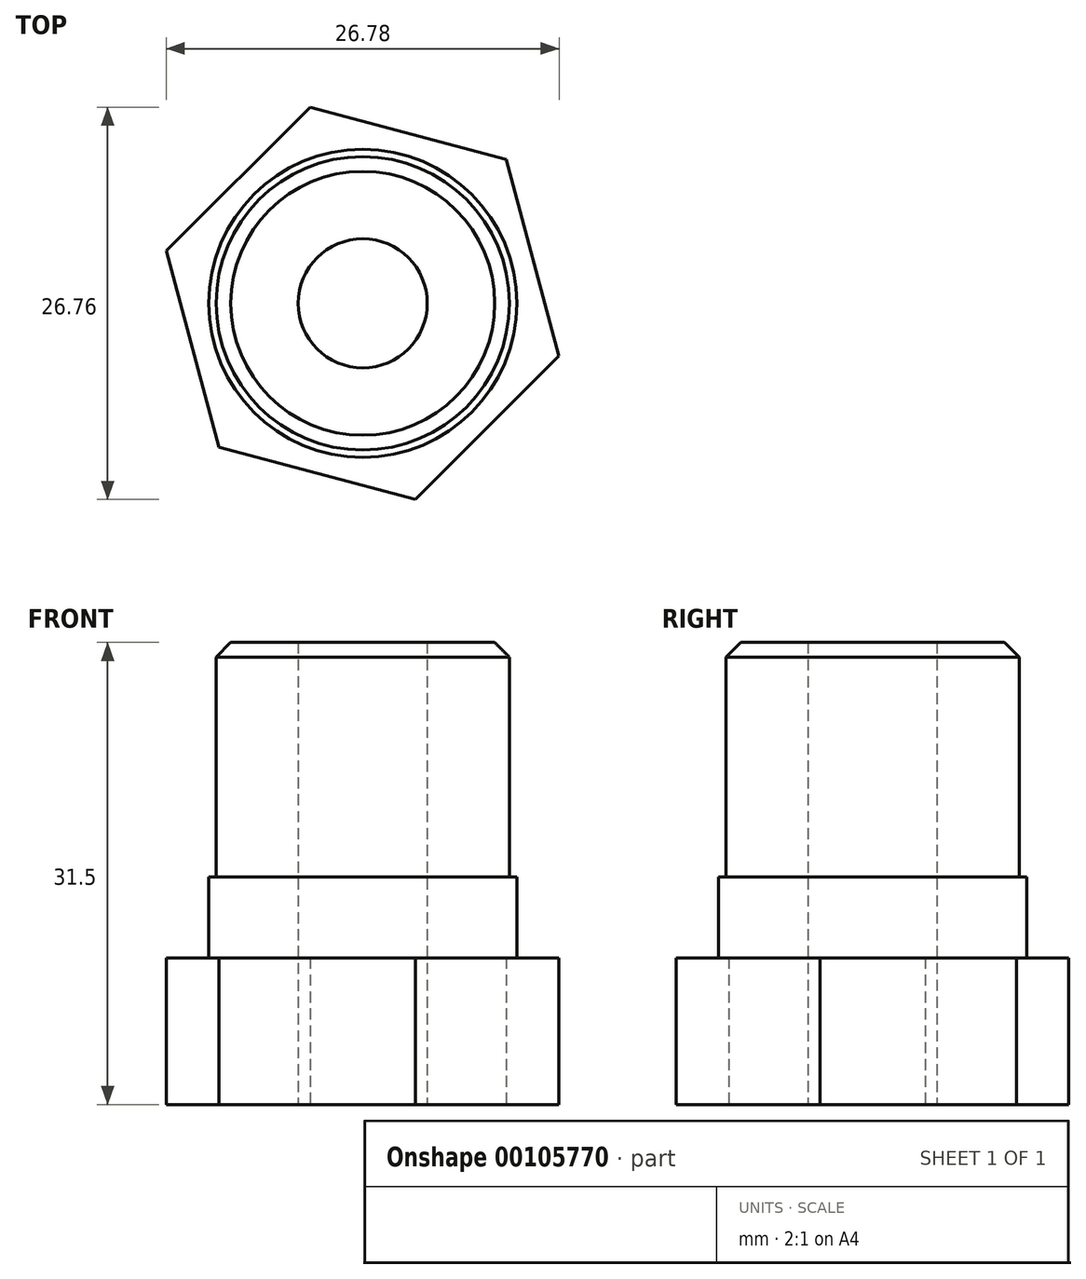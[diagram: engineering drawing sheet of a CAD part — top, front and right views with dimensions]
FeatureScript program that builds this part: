
annotation { "Feature Type Name" : "Feature", "Feature Type Description" : "" }
export const myFeature = defineFeature(function(context is Context, id is Id, definition is map)
    precondition{}
    {
        {
            var Q0;
            Q0=qCreatedBy(makeId("Top.planeOp"),FACE);
            var sketch = newSketch(context, id + "F0", { "sketchPlane" : qUnion([Q0])});
            skCircle(sketch, "E0.cCircle", {"center": v(0, 0) * mm, "radius": 12 * mm, "construction": true});
            skLineSegment(sketch, "E0.0", {"start": v(13.39, -3.58) * mm, "end": v(3.6, -13.38) * mm});
            skLineSegment(sketch, "E0.1", {"start": v(3.6, -13.38) * mm, "end": v(-9.8, -9.8) * mm});
            skLineSegment(sketch, "E0.2", {"start": v(-9.8, -9.8) * mm, "end": v(-13.39, 3.58) * mm});
            skLineSegment(sketch, "E0.3", {"start": v(-13.39, 3.58) * mm, "end": v(-3.6, 13.38) * mm});
            skLineSegment(sketch, "E0.4", {"start": v(-3.6, 13.38) * mm, "end": v(9.8, 9.8) * mm});
            skLineSegment(sketch, "E0.5", {"start": v(9.8, 9.8) * mm, "end": v(13.39, -3.58) * mm});
            skPoint(sketch, "E0.0.midPoint", {"position": v(8.5, -8.48) * mm});
            skSolve(sketch);
        }
        {
            var Q0;
            Q0=makeQuery(id+"F0.imprint","IMPRINT",FACE,{"disambiguationData":[TD([[makeQuery(id+"F0.imprint","IMPRINT",EDGE,{"derivedFrom":sQuery(id+"F0.wireOp",EDGE,"E0.0")}),-1.0]])]});
            extrude(context, id + "F1", {"entities" : qUnion([Q0]), "depth" : 10 * mm});
        }
        {
            var Q0;
            Q0=makeQuery(id+"F1.opExtrude","CAP_FACE",FACE,{"disambiguationData":[OSD([sQuery(id+"F0.wireOp",EDGE,"E0.0"),sQuery(id+"F0.wireOp",EDGE,"E0.1"),sQuery(id+"F0.wireOp",EDGE,"E0.2"),sQuery(id+"F0.wireOp",EDGE,"E0.3"),sQuery(id+"F0.wireOp",EDGE,"E0.4"),sQuery(id+"F0.wireOp",EDGE,"E0.5")])],"isStart":false});
            var sketch = newSketch(context, id + "F2", { "sketchPlane" : qUnion([Q0])});
            skCircle(sketch, "E1", {"center": v(0, 0) * mm, "radius": 10.5 * mm});
            skSolve(sketch);
        }
        {
            var Q0;
            Q0=makeQuery(id+"F2.imprint","IMPRINT",FACE,{"disambiguationData":[TD([[makeQuery(id+"F2.imprint","IMPRINT",EDGE,{"derivedFrom":sQuery(id+"F2.wireOp",EDGE,"E1")}),1.0]])]});
            extrude(context, id + "F3", {"entities" : qUnion([Q0]), "operationType" : NewBodyOperationType.ADD, "depth" : 5.5 * mm});
        }
        {
            var Q0;
            Q0=makeQuery(id+"F3.opExtrude","CAP_FACE",FACE,{"disambiguationData":[OSD([sQuery(id+"F2.wireOp",EDGE,"E1")])],"isStart":false});
            var sketch = newSketch(context, id + "F4", { "sketchPlane" : qUnion([Q0])});
            skCircle(sketch, "E2", {"center": v(0, 0) * mm, "radius": 10 * mm});
            skSolve(sketch);
        }
        {
            var Q0;
            Q0=makeQuery(id+"F4.imprint","IMPRINT",FACE,{"disambiguationData":[TD([[makeQuery(id+"F4.imprint","IMPRINT",EDGE,{"derivedFrom":sQuery(id+"F4.wireOp",EDGE,"E2")}),1.0]])]});
            extrude(context, id + "F5", {"entities" : qUnion([Q0]), "operationType" : NewBodyOperationType.ADD, "depth" : 16 * mm});
        }
        {
            var Q0;
            Q0=makeQuery(id+"F5.opExtrude","CAP_EDGE",EDGE,{"disambiguationData":[OSD([sQuery(id+"F4.wireOp",EDGE,"E2")])],"isStart":false});
            chamfer(context, id + "F6", {"entities" : qUnion([Q0]), "width" : 1 * mm, "tangentPropagation" : true});
        }
        {
            var Q0;
            Q0=makeQuery(id+"F1.opExtrude","CAP_FACE",FACE,{"disambiguationData":[OSD([sQuery(id+"F0.wireOp",EDGE,"E0.0"),sQuery(id+"F0.wireOp",EDGE,"E0.1"),sQuery(id+"F0.wireOp",EDGE,"E0.2"),sQuery(id+"F0.wireOp",EDGE,"E0.3"),sQuery(id+"F0.wireOp",EDGE,"E0.4"),sQuery(id+"F0.wireOp",EDGE,"E0.5")])],"isStart":true});
            var sketch = newSketch(context, id + "F7", { "sketchPlane" : qUnion([Q0])});
            skPoint(sketch, "E3", {"position": v(0, 0) * mm});
            skSolve(sketch);
        }
        {
            var Q0;
            Q0=sQuery(id+"F7.wireOp",VERTEX,"E3");
            var Q1;
            Q1=makeQuery(id+"F1.opExtrude","SWEPT_BODY",BODY,{"disambiguationData":[OSD([sQuery(id+"F0.wireOp",EDGE,"E0.0"),sQuery(id+"F0.wireOp",EDGE,"E0.1"),sQuery(id+"F0.wireOp",EDGE,"E0.2"),sQuery(id+"F0.wireOp",EDGE,"E0.3"),sQuery(id+"F0.wireOp",EDGE,"E0.4"),sQuery(id+"F0.wireOp",EDGE,"E0.5")])]});
            hole(context, id + "F8", {"style" : HoleStyle.SIMPLE, "endStyle" : HoleEndStyle.THROUGH, "standardTappedOrClearance" : lookupTablePath({ "standard" : "ISO", "fit" : "Normal", "size" : "M8", "type" : "Clearance" }), "standardBlindInLast" : lookupTablePath({ "fit" : "Standard", "standard" : "ISO", "size" : "M8", "type" : "Clearance" }), "holeDiameter" : 8.8 * mm, "locations" : qUnion([Q0]), "scope" : qUnion([Q1]), "isTappedThrough" : true});
        }
    });
